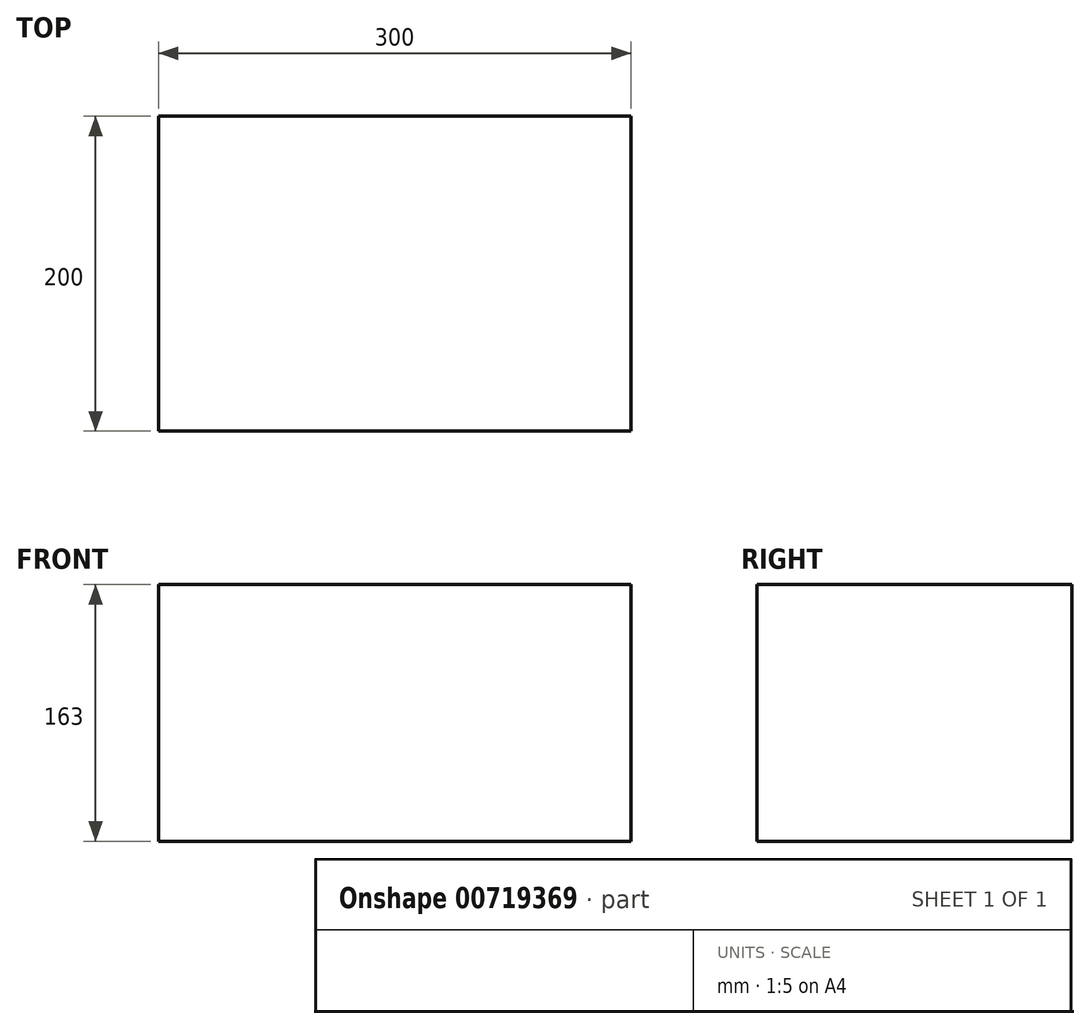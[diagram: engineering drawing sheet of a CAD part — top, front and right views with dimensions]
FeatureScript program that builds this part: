
annotation { "Feature Type Name" : "Feature", "Feature Type Description" : "" }
export const myFeature = defineFeature(function(context is Context, id is Id, definition is map)
    precondition{}
    {
        {
            var Q0;
            Q0=qCreatedBy(makeId("Top.planeOp"),FACE);
            var sketch = newSketch(context, id + "F0", { "sketchPlane" : qUnion([Q0])});
            skLineSegment(sketch, "E0.bottom", {"start": v(-135.3, 104.16) * mm, "end": v(164.7, 104.16) * mm});
            skLineSegment(sketch, "E0.top", {"start": v(-135.3, -95.84) * mm, "end": v(164.7, -95.84) * mm});
            skLineSegment(sketch, "E0.left", {"start": v(-135.3, 104.16) * mm, "end": v(-135.3, -95.84) * mm});
            skLineSegment(sketch, "E0.right", {"start": v(164.7, 104.16) * mm, "end": v(164.7, -95.84) * mm});
            skSolve(sketch);
        }
        {
            var Q0;
            Q0=makeQuery(id+"F0.imprint","IMPRINT",FACE,{"disambiguationData":[TD([[makeQuery(id+"F0.imprint","IMPRINT",EDGE,{"derivedFrom":sQuery(id+"F0.wireOp",EDGE,"E0.bottom")}),-1.0]])]});
            extrude(context, id + "F1", {"entities" : qUnion([Q0]), "depth" : 163 * mm, "offsetDistance" : 25 * mm});
        }
    });
